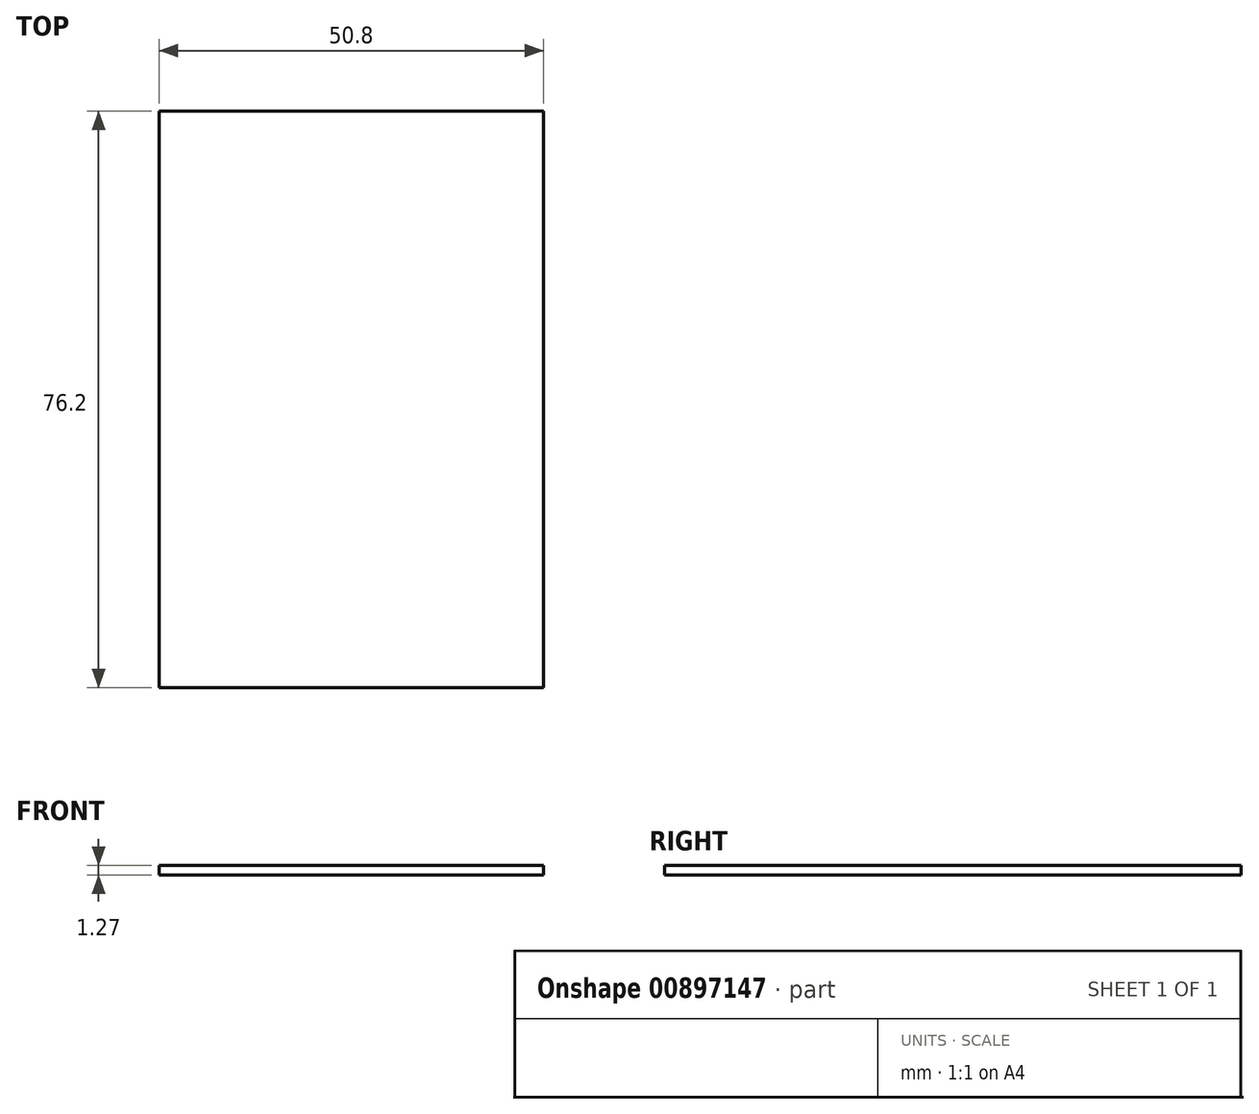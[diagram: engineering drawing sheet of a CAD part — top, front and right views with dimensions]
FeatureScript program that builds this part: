
annotation { "Feature Type Name" : "Feature", "Feature Type Description" : "" }
export const myFeature = defineFeature(function(context is Context, id is Id, definition is map)
    precondition{}
    {
        {
            var Q0;
            Q0=qCreatedBy(makeId("Top.planeOp"),FACE);
            var sketch = newSketch(context, id + "F0", { "sketchPlane" : qUnion([Q0])});
            skLineSegment(sketch, "E0.bottom", {"start": v(0, 0) * mm, "end": v(50.8, 0) * mm});
            skLineSegment(sketch, "E0.top", {"start": v(0, -76.2) * mm, "end": v(50.8, -76.2) * mm});
            skLineSegment(sketch, "E0.left", {"start": v(0, 0) * mm, "end": v(0, -76.2) * mm});
            skLineSegment(sketch, "E0.right", {"start": v(50.8, 0) * mm, "end": v(50.8, -76.2) * mm});
            skSolve(sketch);
        }
        {
            var Q0;
            Q0 = qSketchRegion(id + "F0", true);
            extrude(context, id + "F1", {"entities" : qUnion([Q0]), "depth" : 1.27 * mm, "offsetDistance" : 25.4 * mm});
        }
    });
